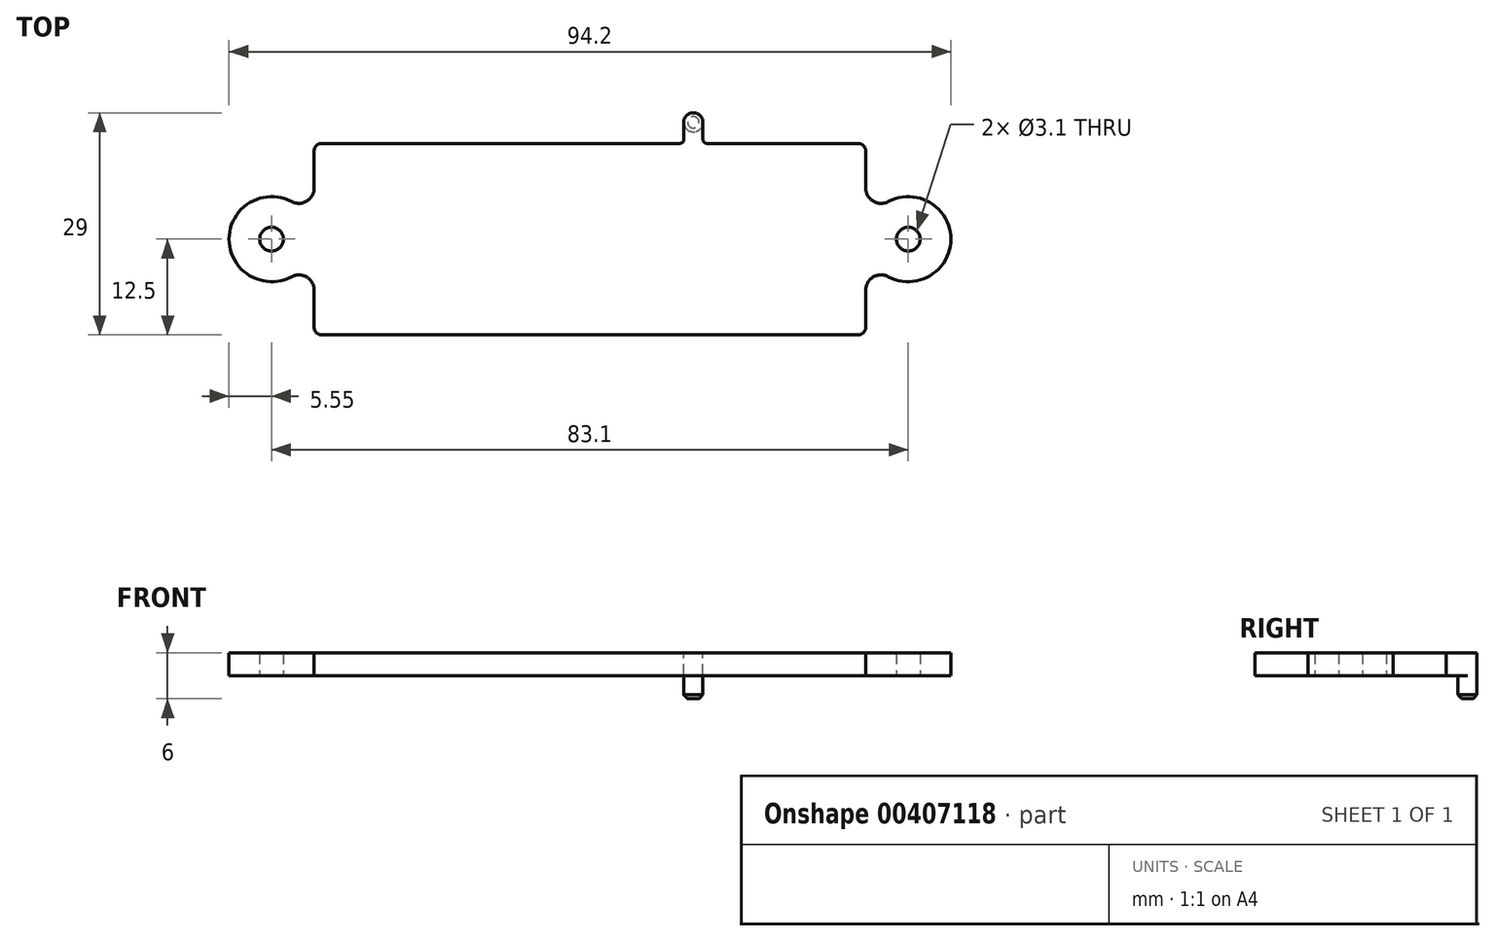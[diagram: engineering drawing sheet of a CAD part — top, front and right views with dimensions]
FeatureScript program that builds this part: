
annotation { "Feature Type Name" : "Feature", "Feature Type Description" : "" }
export const myFeature = defineFeature(function(context is Context, id is Id, definition is map)
    precondition{}
    {
        {
            var Q0;
            Q0=qCreatedBy(makeId("Top.planeOp"),FACE);
            var sketch = newSketch(context, id + "F0", { "sketchPlane" : qUnion([Q0])});
            skLineSegment(sketch, "E0.bottom", {"start": v(-51, 25) * mm, "end": v(19, 25) * mm});
            skLineSegment(sketch, "E0.top", {"start": v(-51, 0) * mm, "end": v(19, 0) * mm});
            skLineSegment(sketch, "E0.left", {"start": v(-52, 24) * mm, "end": v(-52, 1) * mm});
            skLineSegment(sketch, "E0.right", {"start": v(20, 24) * mm, "end": v(20, 1) * mm});
            skLineSegment(sketch, "E1", {"start": v(0, 25) * mm, "end": v(0, 0) * mm, "construction": true});
            skLineSegment(sketch, "E2", {"start": v(0, 12.5) * mm, "end": v(20, 12.5) * mm, "construction": true});
            skLineSegment(sketch, "E3.bottom", {"start": v(0, 25) * mm, "end": v(-28, 25) * mm, "construction": true});
            skLineSegment(sketch, "E3.top", {"start": v(0, 15.5) * mm, "end": v(-28, 15.5) * mm, "construction": true});
            skLineSegment(sketch, "E3.left", {"start": v(0, 25) * mm, "end": v(0, 15.5) * mm, "construction": true});
            skLineSegment(sketch, "E3.right", {"start": v(-28, 25) * mm, "end": v(-28, 15.5) * mm, "construction": true});
            skCircle(sketch, "E4", {"center": v(25.55, 12.5) * mm, "radius": 1.55 * mm});
            skCircle(sketch, "E5", {"center": v(-57.55, 12.5) * mm, "radius": 1.55 * mm});
            skArc(sketch, "E6", {"start": v(-54.94, 17.4) * mm, "mid": v(-63.1, 12.5) * mm, "end": v(-54.94, 7.6) * mm});
            skArc(sketch, "E7", {"start": v(22.94, 7.6) * mm, "mid": v(31.1, 12.5) * mm, "end": v(22.94, 17.4) * mm});
            skArc(sketch, "E8", {"start": v(-54.94, 17.4) * mm, "mid": v(-52.97, 17.45) * mm, "end": v(-52, 19.16) * mm});
            skArc(sketch, "E9", {"start": v(-52, 5.84) * mm, "mid": v(-52.97, 7.55) * mm, "end": v(-54.94, 7.6) * mm});
            skArc(sketch, "E10", {"start": v(20, 19.16) * mm, "mid": v(20.97, 17.45) * mm, "end": v(22.94, 17.4) * mm});
            skArc(sketch, "E11", {"start": v(22.94, 7.6) * mm, "mid": v(20.97, 7.55) * mm, "end": v(20, 5.84) * mm});
            skLineSegment(sketch, "E12.bottom", {"start": v(-45, 25) * mm, "end": v(-5, 25) * mm, "construction": true});
            skLineSegment(sketch, "E12.top", {"start": v(-45, -5) * mm, "end": v(-5, -5) * mm, "construction": true});
            skLineSegment(sketch, "E12.left", {"start": v(-45, 25) * mm, "end": v(-45, -5) * mm, "construction": true});
            skLineSegment(sketch, "E12.right", {"start": v(-5, 25) * mm, "end": v(-5, -5) * mm, "construction": true});
            skPoint(sketch, "E13.visualSharp", {"position": v(-52, 25) * mm});
            skArc(sketch, "E13.filletArc", {"start": v(-51, 25) * mm, "mid": v(-51.7, 24.7) * mm, "end": v(-52, 24) * mm});
            skPoint(sketch, "E14.visualSharp", {"position": v(20, 25) * mm});
            skArc(sketch, "E14.filletArc", {"start": v(20, 24) * mm, "mid": v(19.7, 24.7) * mm, "end": v(19, 25) * mm});
            skPoint(sketch, "E15.visualSharp", {"position": v(20, 0) * mm});
            skArc(sketch, "E15.filletArc", {"start": v(19, 0) * mm, "mid": v(19.7, 0.3) * mm, "end": v(20, 1) * mm});
            skPoint(sketch, "E16.visualSharp", {"position": v(-52, 0) * mm});
            skArc(sketch, "E16.filletArc", {"start": v(-52, 1) * mm, "mid": v(-51.7, 0.3) * mm, "end": v(-51, 0) * mm});
            skSolve(sketch);
        }
        {
            var Q0;
            Q0 = qSketchRegion(id + "F0", true);
            extrude(context, id + "F1", {"entities" : qUnion([Q0]), "depth" : 3 * mm});
        }
        {
            var Q0;
            Q0=makeQuery(id+"F1.opExtrude","CAP_FACE",FACE,{"disambiguationData":[OSD([sQuery(id+"F0.wireOp",EDGE,"E0.bottom"),sQuery(id+"F0.wireOp",EDGE,"E0.top"),sQuery(id+"F0.wireOp",EDGE,"E0.left"),sQuery(id+"F0.wireOp",EDGE,"E0.right"),sQuery(id+"F0.wireOp",EDGE,"E4"),sQuery(id+"F0.wireOp",EDGE,"E5"),sQuery(id+"F0.wireOp",EDGE,"E6"),sQuery(id+"F0.wireOp",EDGE,"E7"),sQuery(id+"F0.wireOp",EDGE,"E8"),sQuery(id+"F0.wireOp",EDGE,"E9"),sQuery(id+"F0.wireOp",EDGE,"E10"),sQuery(id+"F0.wireOp",EDGE,"E11"),sQuery(id+"F0.wireOp",EDGE,"E13.filletArc"),sQuery(id+"F0.wireOp",EDGE,"E14.filletArc"),sQuery(id+"F0.wireOp",EDGE,"E15.filletArc"),sQuery(id+"F0.wireOp",EDGE,"E16.filletArc")])],"isStart":false});
            var sketch = newSketch(context, id + "F2", { "sketchPlane" : qUnion([Q0])});
            skLineSegment(sketch, "E17.bottom", {"start": v(-3.75, 25) * mm, "end": v(-1.25, 25) * mm});
            skLineSegment(sketch, "E17.left", {"start": v(-3.75, 25.5) * mm, "end": v(-3.75, 27.75) * mm});
            skLineSegment(sketch, "E17.right", {"start": v(-1.25, 25.5) * mm, "end": v(-1.25, 27.75) * mm});
            skPoint(sketch, "E18", {"position": v(-2.5, 25) * mm});
            skLineSegment(sketch, "E19", {"start": v(-5, 22.62) * mm, "end": v(0, 22.62) * mm, "construction": true});
            skPoint(sketch, "E20", {"position": v(-2.5, 22.62) * mm});
            skArc(sketch, "E21", {"start": v(-4.25, 25) * mm, "mid": v(-3.9, 25.15) * mm, "end": v(-3.75, 25.5) * mm});
            skArc(sketch, "E22", {"start": v(-1.25, 25.5) * mm, "mid": v(-1.1, 25.15) * mm, "end": v(-0.75, 25) * mm});
            skLineSegment(sketch, "E23", {"start": v(-4.25, 25) * mm, "end": v(-0.75, 25) * mm});
            skArc(sketch, "E24", {"start": v(-1.25, 27.75) * mm, "mid": v(-2.5, 29) * mm, "end": v(-3.75, 27.75) * mm});
            skSolve(sketch);
        }
        {
            var Q0;
            Q0 = qSketchRegion(id + "F2", true);
            var Q1;
            Q1=makeQuery(id+"F1.opExtrude","CAP_FACE",FACE,{"disambiguationData":[OSD([sQuery(id+"F0.wireOp",EDGE,"E0.bottom"),sQuery(id+"F0.wireOp",EDGE,"E0.top"),sQuery(id+"F0.wireOp",EDGE,"E0.left"),sQuery(id+"F0.wireOp",EDGE,"E0.right"),sQuery(id+"F0.wireOp",EDGE,"E4"),sQuery(id+"F0.wireOp",EDGE,"E5"),sQuery(id+"F0.wireOp",EDGE,"E6"),sQuery(id+"F0.wireOp",EDGE,"E7"),sQuery(id+"F0.wireOp",EDGE,"E8"),sQuery(id+"F0.wireOp",EDGE,"E9"),sQuery(id+"F0.wireOp",EDGE,"E10"),sQuery(id+"F0.wireOp",EDGE,"E11"),sQuery(id+"F0.wireOp",EDGE,"E13.filletArc"),sQuery(id+"F0.wireOp",EDGE,"E14.filletArc"),sQuery(id+"F0.wireOp",EDGE,"E15.filletArc"),sQuery(id+"F0.wireOp",EDGE,"E16.filletArc")])],"isStart":true});
            extrude(context, id + "F3", {"entities" : qUnion([Q0]), "operationType" : NewBodyOperationType.ADD, "endBound" : BoundingType.UP_TO_SURFACE, "oppositeDirection" : true, "endBoundEntityFace" : qUnion([Q1]), "depth" : 25 * mm});
        }
        {
            var Q0;
            {var subQ0=sQuery(id+"F0.wireOp",EDGE,"E16.filletArc");var subQ1=sQuery(id+"F0.wireOp",EDGE,"E15.filletArc");var subQ2=sQuery(id+"F0.wireOp",EDGE,"E14.filletArc");var subQ3=sQuery(id+"F0.wireOp",EDGE,"E13.filletArc");var subQ4=sQuery(id+"F0.wireOp",EDGE,"E11");var subQ5=sQuery(id+"F0.wireOp",EDGE,"E10");var subQ6=sQuery(id+"F0.wireOp",EDGE,"E9");var subQ7=sQuery(id+"F0.wireOp",EDGE,"E8");var subQ8=sQuery(id+"F0.wireOp",EDGE,"E7");var subQ9=sQuery(id+"F0.wireOp",EDGE,"E6");var subQ10=sQuery(id+"F0.wireOp",EDGE,"E5");var subQ11=sQuery(id+"F0.wireOp",EDGE,"E4");var subQ12=sQuery(id+"F0.wireOp",EDGE,"E0.right");var subQ13=sQuery(id+"F0.wireOp",EDGE,"E0.left");var subQ14=sQuery(id+"F0.wireOp",EDGE,"E0.top");var subQ15=sQuery(id+"F0.wireOp",EDGE,"E0.bottom");Q0=makeQuery(id+"F3.boolean.opBoolean","MERGE",FACE,{"derivedFrom":[makeQuery(id+"F1.opExtrude","CAP_FACE",FACE,{"disambiguationData":[OSD([subQ15,subQ14,subQ13,subQ12,subQ11,subQ10,subQ9,subQ8,subQ7,subQ6,subQ5,subQ4,subQ3,subQ2,subQ1,subQ0])],"isStart":true}),makeQuery(id+"F3.opExtrude","CAP_FACE",FACE,{"disambiguationData":[OSD([subQ15,subQ14,subQ13,subQ12,subQ11,subQ10,subQ9,subQ8,subQ7,subQ6,subQ5,subQ4,subQ3,subQ2,subQ1,subQ0])],"isStart":false})]});}
            var sketch = newSketch(context, id + "F4", { "sketchPlane" : qUnion([Q0])});
            skCircle(sketch, "E25", {"center": v(-2.5, -27.75) * mm, "radius": 1.25 * mm});
            skSolve(sketch);
        }
        {
            var Q0;
            Q0 = qSketchRegion(id + "F4", true);
            extrude(context, id + "F5", {"entities" : qUnion([Q0]), "operationType" : NewBodyOperationType.ADD, "depth" : 3 * mm});
        }
        {
            var Q0;
            Q0=makeQuery(id+"F5.opExtrude","CAP_EDGE",EDGE,{"disambiguationData":[OSD([sQuery(id+"F4.wireOp",EDGE,"E25")])],"isStart":false});
            chamfer(context, id + "F6", {"entities" : qUnion([Q0]), "width" : 0.5 * mm, "tangentPropagation" : true});
        }
    });
